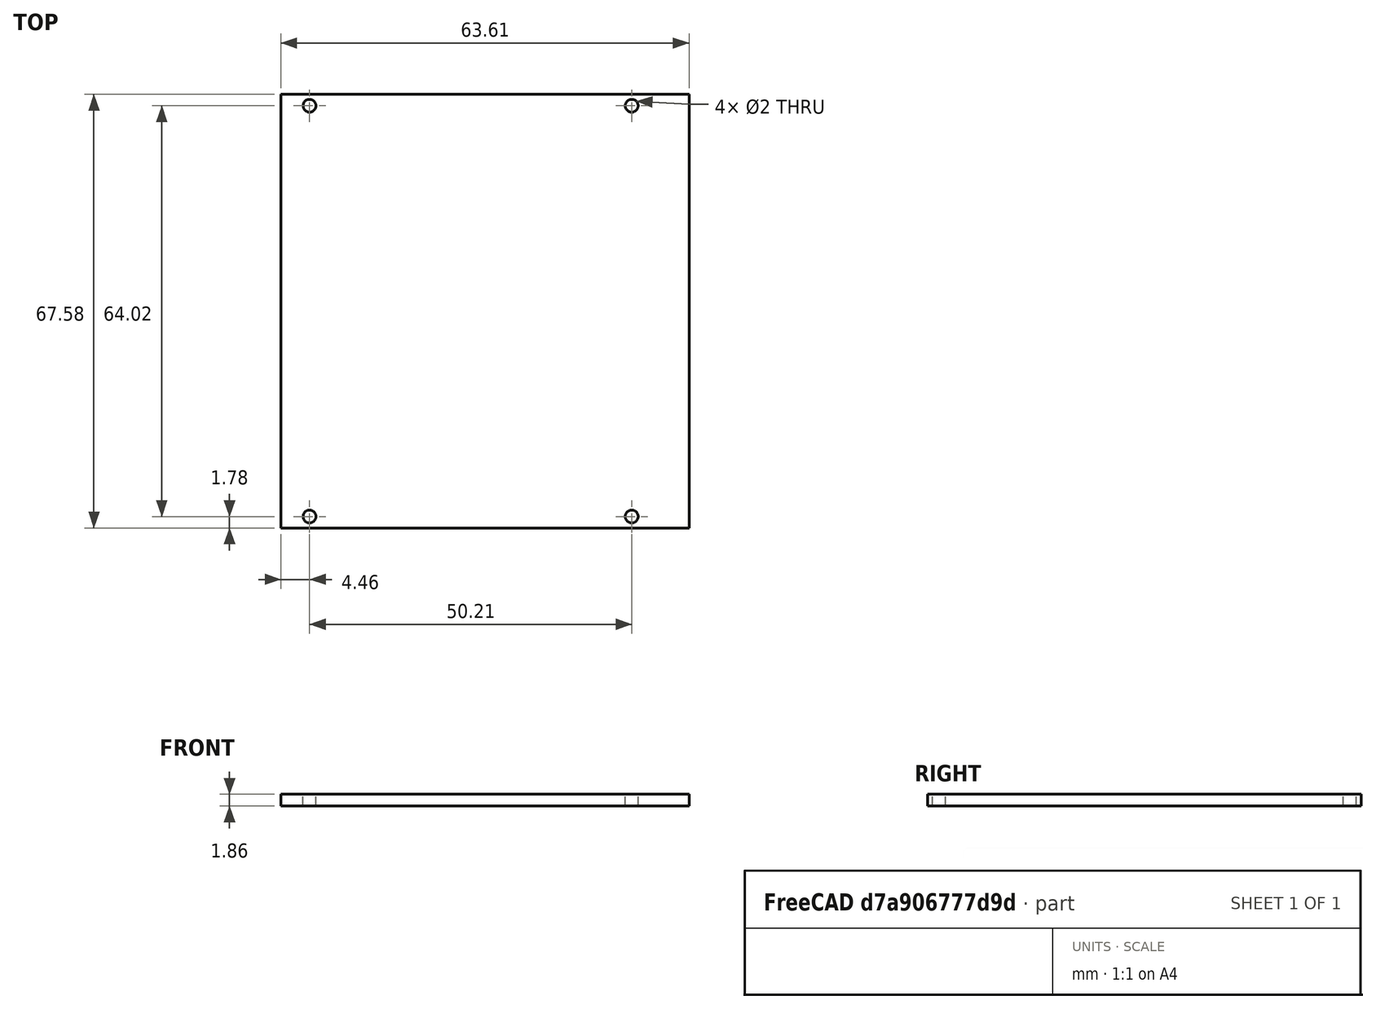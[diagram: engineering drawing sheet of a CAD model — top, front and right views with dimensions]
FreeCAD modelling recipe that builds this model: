
FCSTD DOCUMENT  (FreeCAD 0.15R4671 (Git))
Label: smps_to_dyna_case_top
License: All rights reserved
LicenseURL: http://en.wikipedia.org/wiki/All_rights_reserved
objects: Part::Cylinder×5, Part::Cut×5, Part::Box×1
note: 11 computed .brp shape members not serialized (recipe doc carries the construction recipe); baked Part::Feature solids carry a one-line shape summary decoded from their .brp

FEATURE [Part::Cylinder] Cylinder  label="Cilindro018"
  Angle = 360
  Height = 30
  Placement = pos=(37.23,80,13) rot=(1,0,0;1.5708rad)
  Radius = 7
FEATURE [Part::Cylinder] Cylinder001  label="4001"
  Angle = 360
  Height = 40
  Placement = pos=(4.46,1.78,15.4) rot=(0,0,1;0rad)
  Radius = 1
FEATURE [Part::Cylinder] Cylinder002  label="1001"
  Angle = 360
  Height = 40
  Placement = pos=(54.67,1.78,15.4) rot=(0,0,1;0rad)
  Radius = 1
FEATURE [Part::Cylinder] Cylinder003  label="3001"
  Angle = 360
  Height = 40
  Placement = pos=(4.46,65.8,15.4) rot=(0,0,1;0rad)
  Radius = 1
FEATURE [Part::Cylinder] Cylinder004  label="2001"
  Angle = 360
  Height = 40
  Placement = pos=(54.67,65.8,15.4) rot=(0,0,1;0rad)
  Radius = 1
FEATURE [Part::Box] Box  label="top"
  Height = 1.86
  Length = 63.61
  Placement = pos=(0,0,21.26) rot=(0,0,1;0rad)
  Width = 67.58
FEATURE [Part::Cut] Cut
  Base = -> Box
  Tool = -> Cylinder
FEATURE [Part::Cut] Cut001
  Base = -> Cut
  Tool = -> Cylinder002
FEATURE [Part::Cut] Cut002
  Base = -> Cut001
  Tool = -> Cylinder004
FEATURE [Part::Cut] Cut003
  Base = -> Cut002
  Tool = -> Cylinder003
FEATURE [Part::Cut] Cut004  label="top001"
  Base = -> Cut003
  Tool = -> Cylinder001
